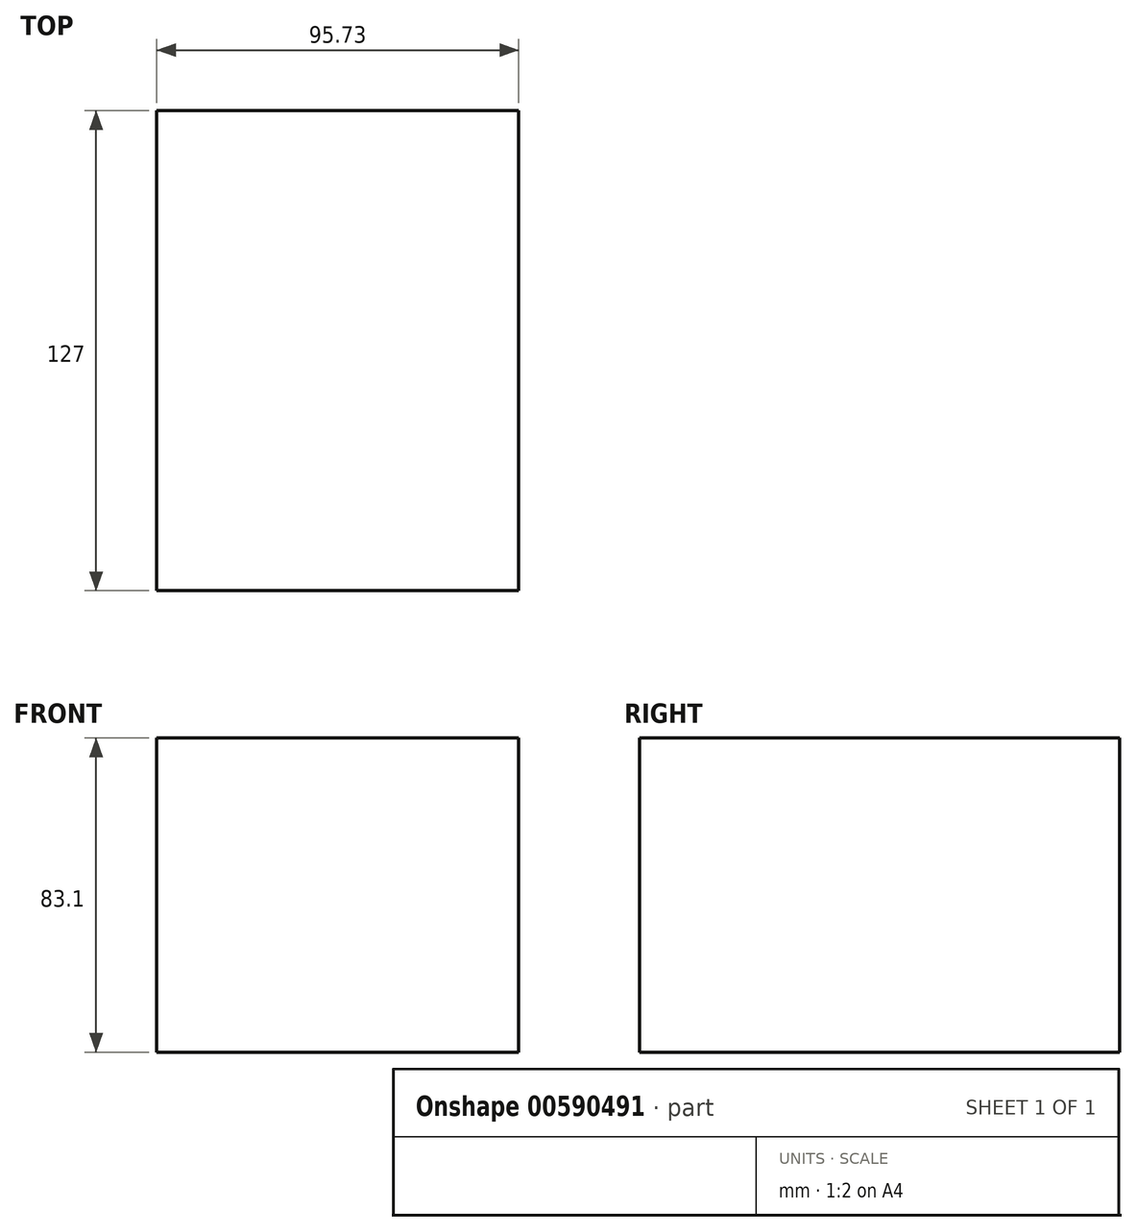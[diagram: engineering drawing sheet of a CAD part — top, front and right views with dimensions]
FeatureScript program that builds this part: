
annotation { "Feature Type Name" : "Feature", "Feature Type Description" : "" }
export const myFeature = defineFeature(function(context is Context, id is Id, definition is map)
    precondition{}
    {
        {
            var Q0;
            Q0=qCreatedBy(makeId("Front.planeOp"),FACE);
            var sketch = newSketch(context, id + "F0", { "sketchPlane" : qUnion([Q0])});
            skLineSegment(sketch, "E0.bottom", {"start": v(0, 0) * mm, "end": v(-95.73, 0) * mm});
            skLineSegment(sketch, "E0.top", {"start": v(0, 83.1) * mm, "end": v(-95.73, 83.1) * mm});
            skLineSegment(sketch, "E0.left", {"start": v(0, 0) * mm, "end": v(0, 83.1) * mm});
            skLineSegment(sketch, "E0.right", {"start": v(-95.73, 0) * mm, "end": v(-95.73, 83.1) * mm});
            skSolve(sketch);
        }
        {
            var Q0;
            Q0 = qSketchRegion(id + "F0", true);
            extrude(context, id + "F1", {"entities" : qUnion([Q0]), "depth" : 127 * mm, "offsetDistance" : 25.4 * mm});
        }
    });
